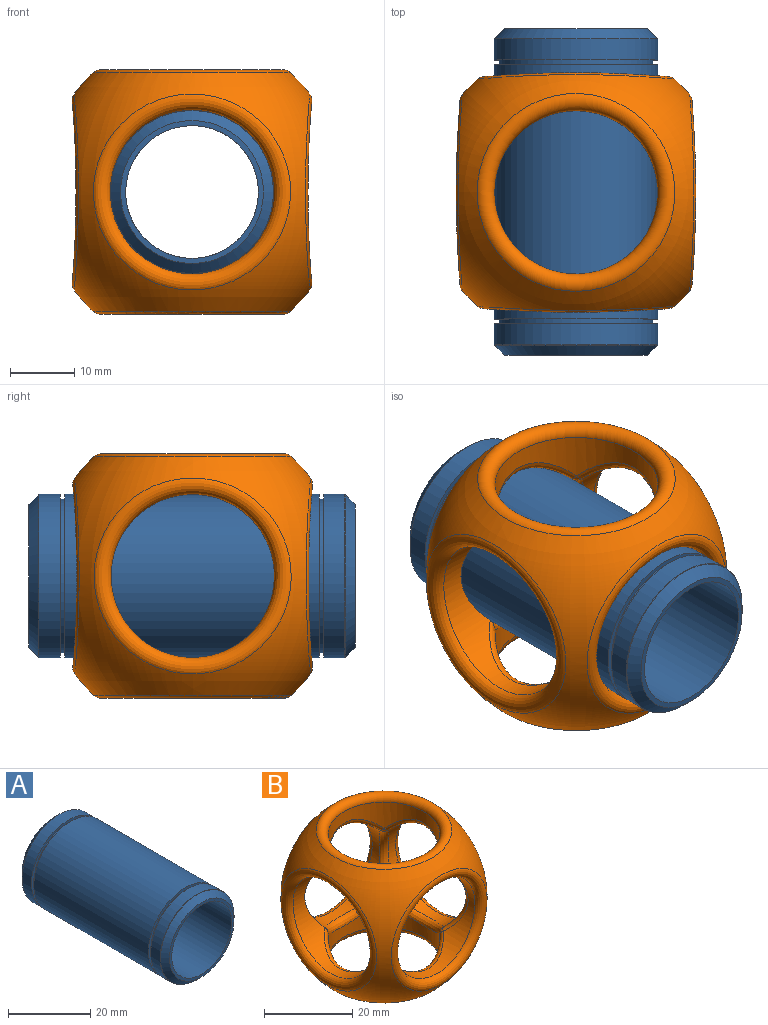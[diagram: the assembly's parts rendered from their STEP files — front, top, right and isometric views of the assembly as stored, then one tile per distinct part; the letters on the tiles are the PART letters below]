
ASSEMBLY  parts=2 mates=1
PART A: 15 faces, bbox 27.5x50.8x27.5 mm
  f0: cylinder r=12.7mm len=25.4mm, axis (0,1,0), area 258.3mm2, adj f4,f13
  f1: plane 22.23x22.23mm, normal (0,-1,0), area 53.4mm2, adj f2,f14
  f2: cone r=11.11mm half-angle=45deg, axis (0,1,0), area 163.8mm2, adj f1,f13
  f3: plane 25.4x25.4mm, normal (0,-1,0), area 59mm2, adj f5,f6
  f4: plane 25.4x25.4mm, normal (0,1,0), area 59mm2, adj f0,f5
  f5: cylinder r=11.94mm len=23.88mm, axis (0,-1,0), area 57.2mm2, adj f3,f4
  f6: cylinder r=12.7mm len=39.52mm, axis (0,1,0), area 3153.7mm2, adj f3,f7
  f7: plane 25.4x25.4mm, normal (0,1,0), area 59mm2, adj f6,f9
  f8: plane 25.4x25.4mm, normal (0,-1,0), area 59mm2, adj f9,f12
  f9: cylinder r=11.94mm len=23.88mm, axis (0,-1,0), area 57.2mm2, adj f7,f8
  f10: plane 22.23x22.23mm, normal (0,1,0), area 53.4mm2, adj f11,f14
  f11: cone r=12.7mm half-angle=45deg, axis (0,-1,0), area 168mm2, adj f10,f12
  f12: cylinder r=12.7mm len=25.4mm, axis (0,1,0), area 262.5mm2, adj f8,f11
  f13: torus R=12.57mm, axis (0,-1,0), area 8mm2, adj f0,f2
  f14: cylinder r=10.32mm len=50.8mm, axis (0,-1,0), area 3293.6mm2, adj f1,f10
PART B: 30 faces, bbox 46.8x46.8x38 mm
  f0: revolved ~46.77x46.77mm, area 2112mm2, adj f7,f8,f26,f27,f28,f29
  f1: cylinder r=12.7mm len=25.4mm, axis (0,0,-1), area 361.6mm2, adj f18,f21,f24,f25,f28
  f2: cylinder r=12.7mm len=25.4mm, axis (0,0,-1), area 374.9mm2, adj f10,f11,f12,f13,f29
  f3: cylinder r=12.7mm len=25.4mm, axis (1,0,0), area 332.8mm2, adj f6,f11,f19,f24,f27
  f4: cylinder r=12.7mm len=25.4mm, axis (-1,0,0), area 309.5mm2, adj f13,f14,f20,f21,f26
  f5: cylinder r=12.7mm len=25.4mm, axis (0,1,0), area 305.4mm2, adj f7,f10,f14,f18,f19
  f6: cylinder r=12.7mm len=25.4mm, axis (0,1,0), area 372.1mm2, adj f3,f8,f12,f20,f25
  f7: bspline ~30.66x30.49mm, area 308.5mm2, adj f0,f5
  f8: bspline ~30.66x30.49mm, area 308.5mm2, adj f0,f6
  f9: sphere r=1.59mm, area 1.3mm2, adj f10,f13,f14
  f10: bspline ~17.96x5.31mm, area 46.9mm2, adj f2,f5,f9,f15
  f11: bspline ~18.47x5.85mm, area 47.7mm2, adj f2,f3,f12,f15
  f12: bspline ~18.47x5.85mm, area 47.7mm2, adj f2,f6,f11,f16
  f13: bspline ~17.96x5.31mm, area 46.9mm2, adj f2,f4,f9,f16
  f14: bspline ~17.96x5.31mm, area 46.9mm2, adj f4,f5,f9,f17
  f15: sphere r=1.59mm, area 1.3mm2, adj f10,f11,f19
  f16: sphere r=1.59mm, area 1.3mm2, adj f12,f13,f20
  f17: sphere r=1.59mm, area 1.3mm2, adj f14,f18,f21
  f18: bspline ~17.96x5.31mm, area 46.9mm2, adj f1,f5,f17,f22
  f19: bspline ~17.96x5.31mm, area 46.9mm2, adj f3,f5,f15,f22
  f20: bspline ~17.96x5.31mm, area 46.9mm2, adj f4,f6,f16,f23
  f21: bspline ~17.96x5.31mm, area 46.9mm2, adj f1,f4,f17,f23
  f22: sphere r=1.59mm, area 1.3mm2, adj f18,f19,f24
  f23: sphere r=1.59mm, area 1.3mm2, adj f20,f21,f25
  f24: bspline ~18.47x5.85mm, area 47.7mm2, adj f1,f3,f22,f25
  f25: bspline ~18.47x5.85mm, area 47.7mm2, adj f1,f6,f23,f24
  f26: bspline ~30.66x30.48mm, area 308.5mm2, adj f0,f4
  f27: bspline ~30.67x30.48mm, area 308.5mm2, adj f0,f3
  f28: torus R=14.29mm, axis (0,0,1), area 320mm2, adj f0,f1
  f29: torus R=14.29mm, axis (0,0,-1), area 320mm2, adj f0,f2
PLACE A t=(-10.53,25.59,15.27)mm
PLACE B t=(-10.53,0.09,-10.13)mm
MATE cylindrical A.f0 <-> B.f5  axis (0,1,0) through (-10.53,0.19,15.27)mm
